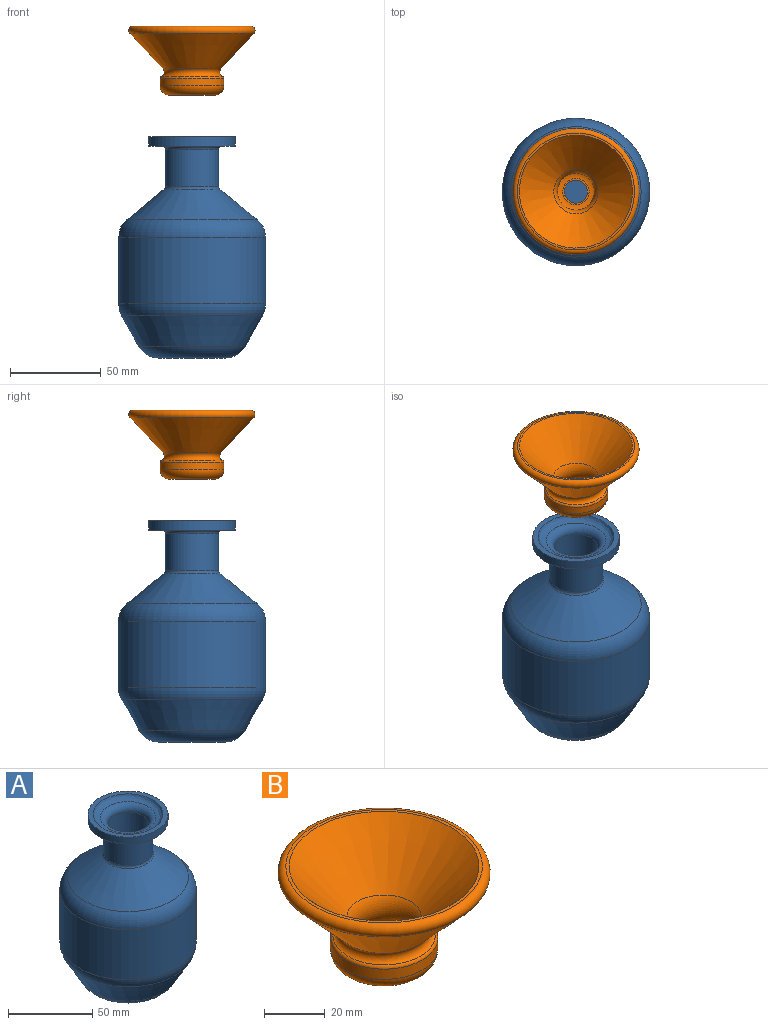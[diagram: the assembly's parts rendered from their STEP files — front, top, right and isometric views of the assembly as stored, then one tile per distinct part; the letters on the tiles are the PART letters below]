
ASSEMBLY  parts=2 mates=2
PART A: 24 faces, bbox 87.9x87.9x124.5 mm
  f0: torus R=16.63mm, axis (0,0,1), area 162.6mm2, adj f1,f12
  f1: cylinder r=14.67mm len=29.34mm, axis (0,0,1), area 1873.2mm2, adj f0,f2
  f2: torus R=16.63mm, axis (0,0,1), area 297.7mm2, adj f1,f3
  f3: plane 47.62x47.62mm, normal (0,0,-1), area 912mm2, adj f2,f4
  f4: cylinder r=23.81mm len=47.62mm, axis (0,0,1), area 754.8mm2, adj f3,f5
  f5: plane 47.67x47.67mm, normal (0,0,1), area 420.6mm2, adj f4,f23
  f6: plane 36.57x36.57mm, normal (0,0,-1), area 1050.1mm2, adj f7
  f7: torus R=18.28mm, axis (0,0,1), area 2059.2mm2, adj f6,f8
  f8: cone r=38.96mm half-angle=29.4deg, axis (0,0,1), area 4204.9mm2, adj f7,f9
  f9: torus R=27.9mm, axis (0,0,1), area 1639.6mm2, adj f8,f10
  f10: cylinder r=40.6mm len=81.2mm, axis (0,0,1), area 9332.2mm2, adj f9,f11
  f11: torus R=27.9mm, axis (0,0,1), area 2754.8mm2, adj f10,f12
  f12: cone r=15.39mm half-angle=50.7deg, axis (0,0,-1), area 4282.1mm2, adj f0,f11
  f13: torus R=16.63mm, axis (0,0,1), area 317.8mm2, adj f14,f22
  f14: cylinder r=12.13mm len=24.26mm, axis (0,0,1), area 1548.9mm2, adj f13,f15
  f15: torus R=16.63mm, axis (0,0,1), area 589.9mm2, adj f14,f23
  f16: plane 36.57x36.57mm, normal (0,0,1), area 1050.1mm2, adj f17
  f17: torus R=18.28mm, axis (0,0,1), area 1564.8mm2, adj f16,f18
  f18: cone r=36.75mm half-angle=29.4deg, axis (0,0,1), area 3932.5mm2, adj f17,f19
  f19: torus R=27.9mm, axis (0,0,1), area 1232.1mm2, adj f18,f20
  f20: cylinder r=38.06mm len=76.12mm, axis (0,0,1), area 8748.3mm2, adj f19,f21
  f21: torus R=27.9mm, axis (0,0,1), area 2078.3mm2, adj f20,f22
  f22: cone r=13.78mm half-angle=50.7deg, axis (0,0,-1), area 4013.8mm2, adj f13,f21
  f23: bspline ~43.65x43.65mm, area 635.1mm2, adj f5,f15
PART B: 13 faces, bbox 75.3x75.3x38.1 mm
  f0: plane 64.47x64.47mm, normal (0,0,1), area 219.1mm2, adj f4,f7
  f1: plane 24.99x24.99mm, normal (0,0,-1), area 363.9mm2, adj f9,f11
  f2: cylinder r=17.58mm len=35.15mm, axis (0,0,1), area 451.9mm2, adj f11,f12
  f3: cone r=11.9mm half-angle=43.2deg, axis (0,0,1), area 4175.3mm2, adj f4,f5
  f4: torus R=32.24mm, axis (0,0,1), area 1263.9mm2, adj f0,f3
  f5: torus R=17.76mm, axis (0,0,-1), area 482.6mm2, adj f3,f12
  f6: plane 14.48x14.48mm, normal (0,0,1), area 38mm2, adj f9,f10
  f7: cone r=8.2mm half-angle=43.2deg, axis (0,0,1), area 3769mm2, adj f0,f8
  f8: torus R=17.76mm, axis (0,0,-1), area 814.4mm2, adj f7,f10
  f9: cylinder r=6.35mm len=12.7mm, axis (0,0,-1), area 202.7mm2, adj f1,f6
  f10: torus R=7.24mm, axis (0,0,-1), area 364.6mm2, adj f6,f8
  f11: torus R=12.5mm, axis (0,0,1), area 788.7mm2, adj f1,f2
  f12: torus R=16.31mm, axis (0,0,-1), area 162.8mm2, adj f2,f5
PLACE A rot(axis=(1,0,0),0deg) t=(0,0,66.35)mm
PLACE B rot(axis=(0,0,-1),30deg) t=(0,0,154.99)mm
MATE cylindrical B.f2 <-> A.f0  axis (0,0,-1) through (0,0,144.83)mm
MATE planar B.f2 <-> A.f0  axis (0,0,-1) through (0,0,144.83)mm
